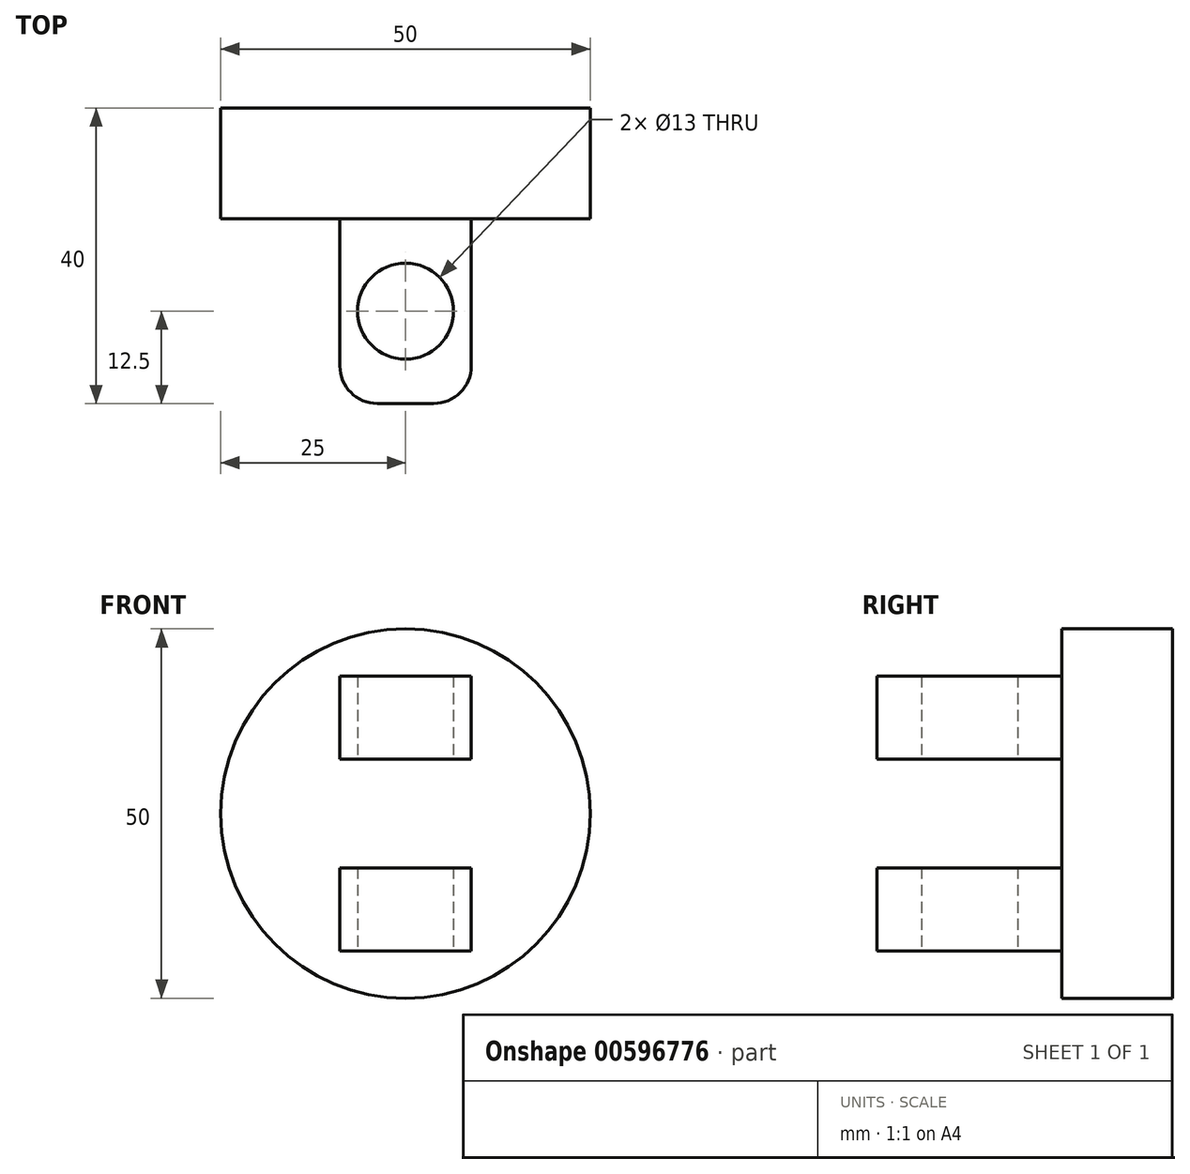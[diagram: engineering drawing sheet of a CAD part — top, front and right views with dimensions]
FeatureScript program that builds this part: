
annotation { "Feature Type Name" : "Feature", "Feature Type Description" : "" }
export const myFeature = defineFeature(function(context is Context, id is Id, definition is map)
    precondition{}
    {
        {
            var Q0;
            Q0=qCreatedBy(makeId("Front.planeOp"),FACE);
            var sketch = newSketch(context, id + "F0", { "sketchPlane" : qUnion([Q0])});
            skCircle(sketch, "E0", {"center": v(0, 0) * mm, "radius": 25 * mm});
            skSolve(sketch);
        }
        {
            var Q0;
            Q0=makeQuery(id+"F0.imprint","IMPRINT",FACE,{"disambiguationData":[TD([[makeQuery(id+"F0.imprint","IMPRINT",EDGE,{"derivedFrom":sQuery(id+"F0.wireOp",EDGE,"E0")}),1.0]])]});
            extrude(context, id + "F1", {"entities" : qUnion([Q0]), "depth" : 15 * mm, "offsetDistance" : 25.4 * mm});
        }
        {
            var Q0;
            Q0=makeQuery(id+"F1.opExtrude","CAP_FACE",FACE,{"disambiguationData":[OSD([sQuery(id+"F0.wireOp",EDGE,"E0")])],"isStart":false});
            var sketch = newSketch(context, id + "F2", { "sketchPlane" : qUnion([Q0])});
            skLineSegment(sketch, "E1.bottom", {"start": v(-8.9, 18.6) * mm, "end": v(8.9, 18.6) * mm});
            skLineSegment(sketch, "E1.top", {"start": v(-8.9, -18.6) * mm, "end": v(8.9, -18.6) * mm});
            skLineSegment(sketch, "E1.left", {"start": v(-8.9, 18.6) * mm, "end": v(-8.9, -18.6) * mm});
            skLineSegment(sketch, "E1.right", {"start": v(8.9, 18.6) * mm, "end": v(8.9, -18.6) * mm});
            skPoint(sketch, "E1.middle", {"position": v(0, 0) * mm});
            skSolve(sketch);
        }
        {
            var Q0;
            Q0=makeQuery(id+"F2.imprint","IMPRINT",FACE,{"disambiguationData":[TD([[makeQuery(id+"F2.imprint","IMPRINT",EDGE,{"derivedFrom":sQuery(id+"F2.wireOp",EDGE,"E1.bottom")}),-1.0]])]});
            extrude(context, id + "F3", {"entities" : qUnion([Q0]), "operationType" : NewBodyOperationType.ADD, "depth" : 25 * mm, "offsetDistance" : 25.4 * mm});
        }
        {
            var Q0;
            Q0=makeQuery(id+"F3.opExtrude","CAP_FACE",FACE,{"disambiguationData":[OSD([sQuery(id+"F2.wireOp",EDGE,"E1.bottom"),sQuery(id+"F2.wireOp",EDGE,"E1.top"),sQuery(id+"F2.wireOp",EDGE,"E1.left"),sQuery(id+"F2.wireOp",EDGE,"E1.right")])],"isStart":false});
            var sketch = newSketch(context, id + "F4", { "sketchPlane" : qUnion([Q0])});
            skLineSegment(sketch, "E2.bottom", {"start": v(8.9, -7.34) * mm, "end": v(-8.9, -7.34) * mm});
            skLineSegment(sketch, "E2.top", {"start": v(8.9, 7.34) * mm, "end": v(-8.9, 7.34) * mm});
            skLineSegment(sketch, "E2.left", {"start": v(8.9, -7.34) * mm, "end": v(8.9, 7.34) * mm});
            skLineSegment(sketch, "E2.right", {"start": v(-8.9, -7.34) * mm, "end": v(-8.9, 7.34) * mm});
            skPoint(sketch, "E2.middle", {"position": v(0, 0) * mm});
            skSolve(sketch);
        }
        {
            var Q0;
            Q0=makeQuery(id+"F3.opExtrude","SWEPT_FACE",FACE,{"disambiguationData":[OSD([sQuery(id+"F2.wireOp",EDGE,"E1.top")])]});
            var sketch = newSketch(context, id + "F5", { "sketchPlane" : qUnion([Q0])});
            skCircle(sketch, "E3", {"center": v(0, 27.5) * mm, "radius": 6.5 * mm});
            skPoint(sketch, "E3.centerSnap0", {"position": v(8.9, 27.5) * mm});
            skSolve(sketch);
        }
        {
            var Q0;
            Q0=sQuery(id+"F5.wireOp",VERTEX,"E3.center");
            var Q1;
            Q1=makeQuery(id+"F1.opExtrude","SWEPT_BODY",BODY,{"disambiguationData":[OSD([sQuery(id+"F0.wireOp",EDGE,"E0")])]});
            hole(context, id + "F6", {"style" : HoleStyle.SIMPLE, "endStyle" : HoleEndStyle.THROUGH, "holeDiameter" : 13 * mm, "majorDiameter" : 6.35 * mm, "isTappedThrough" : true, "tappedDepth" : 12.7 * mm, "tapClearance" : 3, "locations" : qUnion([Q0]), "scope" : qUnion([Q1])});
        }
        {
            var Q0;
            Q0=makeQuery(id+"F4.imprint","IMPRINT",FACE,{"disambiguationData":[TD([[makeQuery(id+"F4.imprint","IMPRINT",EDGE,{"derivedFrom":sQuery(id+"F4.wireOp",EDGE,"E2.bottom")}),-1.0]])]});
            extrude(context, id + "F7", {"entities" : qUnion([Q0]), "operationType" : NewBodyOperationType.REMOVE, "oppositeDirection" : true, "depth" : 25 * mm, "offsetDistance" : 25.4 * mm});
        }
        {
            var Q0;
            {var subQ0=sQuery(id+"F2.wireOp",EDGE,"E1.bottom");var subQ1=sQuery(id+"F2.wireOp",EDGE,"E1.right");Q0=makeQuery(id+"F7.boolean.opBoolean","SPLIT",EDGE,{"disambiguationData":[TD([makeQuery(id+"F3.opExtrude","SWEPT_FACE",FACE,{"disambiguationData":[OSD([subQ0])]})])],"derivedFrom":makeQuery(id+"F3.opExtrude","CAP_EDGE",EDGE,{"disambiguationData":[OSD([subQ1])],"isStart":false})});}
            var Q1;
            {var subQ0=sQuery(id+"F2.wireOp",EDGE,"E1.bottom");var subQ1=sQuery(id+"F2.wireOp",EDGE,"E1.left");Q1=makeQuery(id+"F7.boolean.opBoolean","SPLIT",EDGE,{"disambiguationData":[TD([makeQuery(id+"F3.opExtrude","SWEPT_FACE",FACE,{"disambiguationData":[OSD([subQ0])]})])],"derivedFrom":makeQuery(id+"F3.opExtrude","CAP_EDGE",EDGE,{"disambiguationData":[OSD([subQ1])],"isStart":false})});}
            var Q2;
            {var subQ0=sQuery(id+"F2.wireOp",EDGE,"E1.left");var subQ1=sQuery(id+"F2.wireOp",EDGE,"E1.top");Q2=makeQuery(id+"F7.boolean.opBoolean","SPLIT",EDGE,{"disambiguationData":[TD([makeQuery(id+"F3.opExtrude","SWEPT_FACE",FACE,{"disambiguationData":[OSD([subQ1])]})])],"derivedFrom":makeQuery(id+"F3.opExtrude","CAP_EDGE",EDGE,{"disambiguationData":[OSD([subQ0])],"isStart":false})});}
            var Q3;
            {var subQ0=sQuery(id+"F2.wireOp",EDGE,"E1.right");var subQ1=sQuery(id+"F2.wireOp",EDGE,"E1.top");Q3=makeQuery(id+"F7.boolean.opBoolean","SPLIT",EDGE,{"disambiguationData":[TD([makeQuery(id+"F3.opExtrude","SWEPT_FACE",FACE,{"disambiguationData":[OSD([subQ1])]})])],"derivedFrom":makeQuery(id+"F3.opExtrude","CAP_EDGE",EDGE,{"disambiguationData":[OSD([subQ0])],"isStart":false})});}
            fillet(context, id + "F8", {"entities" : qUnion([Q0, Q1, Q2, Q3]), "radius" : 5.08 * mm, "tangentPropagation" : true, "allowEdgeOverflow" : false});
        }
    });
